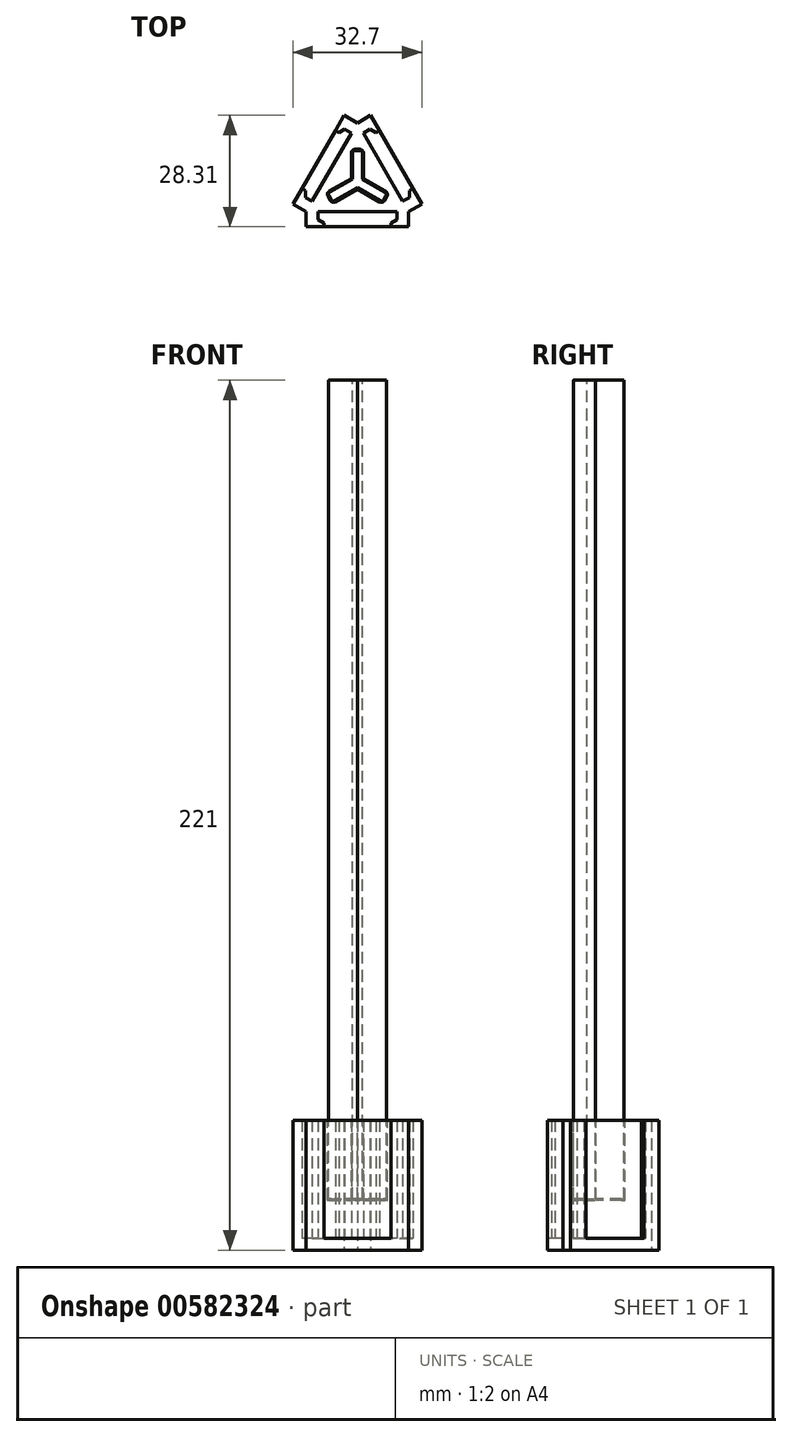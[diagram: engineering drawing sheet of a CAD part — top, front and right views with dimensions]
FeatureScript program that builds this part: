
annotation { "Feature Type Name" : "Feature", "Feature Type Description" : "" }
export const myFeature = defineFeature(function(context is Context, id is Id, definition is map)
    precondition{}
    {
        {
            var Q0;
            Q0=qCreatedBy(makeId("Top.planeOp"),FACE);
            var sketch = newSketch(context, id + "F0", { "sketchPlane" : qUnion([Q0])});
            skLineSegment(sketch, "E0", {"start": v(0, -7.5) * mm, "end": v(10, -7.5) * mm});
            skLineSegment(sketch, "E1", {"start": v(10, -7.5) * mm, "end": v(10, -9.5) * mm});
            skLineSegment(sketch, "E2", {"start": v(10, -9.5) * mm, "end": v(8.5, -10.37) * mm});
            skLineSegment(sketch, "E3", {"start": v(8.5, -10.37) * mm, "end": v(8.5, -11.37) * mm});
            skLineSegment(sketch, "E4", {"start": v(8.5, -11.37) * mm, "end": v(13, -11.37) * mm});
            skLineSegment(sketch, "E5", {"start": v(13, -11.37) * mm, "end": v(13, -7.5) * mm});
            skLineSegment(sketch, "E6.MirrorCS", {"start": v(-13, -11.37) * mm, "end": v(-13, -7.5) * mm});
            skLineSegment(sketch, "E7.MirrorCS", {"start": v(-10, -7.5) * mm, "end": v(-10, -9.5) * mm});
            skLineSegment(sketch, "E8.MirrorCS", {"start": v(0, -7.5) * mm, "end": v(-10, -7.5) * mm});
            skLineSegment(sketch, "E9.MirrorCS", {"start": v(-8.5, -10.37) * mm, "end": v(-8.5, -11.37) * mm});
            skLineSegment(sketch, "E10.MirrorCS", {"start": v(-10, -9.5) * mm, "end": v(-8.5, -10.37) * mm});
            skLineSegment(sketch, "E11.MirrorCS", {"start": v(-8.5, -11.37) * mm, "end": v(-13, -11.37) * mm});
            skLineSegment(sketch, "E12.1.0", {"start": v(6.5, 3.75) * mm, "end": v(11.5, -4.9) * mm});
            skLineSegment(sketch, "E12.1.1", {"start": v(1.5, 12.41) * mm, "end": v(3.23, 13.41) * mm});
            skLineSegment(sketch, "E12.1.2", {"start": v(11.5, -4.9) * mm, "end": v(13.23, -3.9) * mm});
            skLineSegment(sketch, "E12.1.3", {"start": v(14.1, -1.68) * mm, "end": v(16.35, -5.57) * mm});
            skLineSegment(sketch, "E12.1.4", {"start": v(16.35, -5.57) * mm, "end": v(13, -7.5) * mm});
            skLineSegment(sketch, "E12.1.5", {"start": v(5.6, 13.05) * mm, "end": v(3.35, 16.94) * mm});
            skLineSegment(sketch, "E12.1.6", {"start": v(6.5, 3.75) * mm, "end": v(1.5, 12.41) * mm});
            skLineSegment(sketch, "E12.1.7", {"start": v(3.35, 16.94) * mm, "end": v(0, 15.01) * mm});
            skLineSegment(sketch, "E12.1.8", {"start": v(13.23, -2.18) * mm, "end": v(14.1, -1.68) * mm});
            skLineSegment(sketch, "E12.1.9", {"start": v(3.23, 13.41) * mm, "end": v(4.73, 12.55) * mm});
            skLineSegment(sketch, "E12.1.10", {"start": v(13.23, -3.9) * mm, "end": v(13.23, -2.18) * mm});
            skLineSegment(sketch, "E12.1.11", {"start": v(4.73, 12.55) * mm, "end": v(5.6, 13.05) * mm});
            skLineSegment(sketch, "E12.2.0", {"start": v(-6.5, 3.75) * mm, "end": v(-1.5, 12.41) * mm});
            skLineSegment(sketch, "E12.2.1", {"start": v(-11.5, -4.9) * mm, "end": v(-13.23, -3.9) * mm});
            skLineSegment(sketch, "E12.2.2", {"start": v(-1.5, 12.41) * mm, "end": v(-3.23, 13.41) * mm});
            skLineSegment(sketch, "E12.2.3", {"start": v(-5.6, 13.05) * mm, "end": v(-3.35, 16.94) * mm});
            skLineSegment(sketch, "E12.2.4", {"start": v(-3.35, 16.94) * mm, "end": v(0, 15.01) * mm});
            skLineSegment(sketch, "E12.2.5", {"start": v(-14.1, -1.68) * mm, "end": v(-16.35, -5.57) * mm});
            skLineSegment(sketch, "E12.2.6", {"start": v(-6.5, 3.75) * mm, "end": v(-11.5, -4.9) * mm});
            skLineSegment(sketch, "E12.2.7", {"start": v(-16.35, -5.57) * mm, "end": v(-13, -7.5) * mm});
            skLineSegment(sketch, "E12.2.8", {"start": v(-4.73, 12.55) * mm, "end": v(-5.6, 13.05) * mm});
            skLineSegment(sketch, "E12.2.9", {"start": v(-13.23, -3.9) * mm, "end": v(-13.23, -2.18) * mm});
            skLineSegment(sketch, "E12.2.10", {"start": v(-3.23, 13.41) * mm, "end": v(-4.73, 12.55) * mm});
            skLineSegment(sketch, "E12.2.11", {"start": v(-13.23, -2.18) * mm, "end": v(-14.1, -1.68) * mm});
            skPoint(sketch, "E12.center", {"position": v(0, 0) * mm});
            skSolve(sketch);
        }
        {
            var Q0;
            Q0=makeQuery(id+"F0.imprint","IMPRINT",FACE,{"disambiguationData":[TD([[makeQuery(id+"F0.imprint","IMPRINT",EDGE,{"derivedFrom":sQuery(id+"F0.wireOp",EDGE,"E0")}),1.0]])]});
            extrude(context, id + "F1", {"entities" : qUnion([Q0]), "depth" : 30 * mm, "offsetDistance" : 25 * mm});
        }
        {
            var Q0;
            Q0=makeQuery(id+"F1.opExtrude","CAP_FACE",FACE,{"disambiguationData":[OSD([sQuery(id+"F0.wireOp",EDGE,"E0"),sQuery(id+"F0.wireOp",EDGE,"E1"),sQuery(id+"F0.wireOp",EDGE,"E2"),sQuery(id+"F0.wireOp",EDGE,"E3"),sQuery(id+"F0.wireOp",EDGE,"E4"),sQuery(id+"F0.wireOp",EDGE,"E5"),sQuery(id+"F0.wireOp",EDGE,"E6.MirrorCS"),sQuery(id+"F0.wireOp",EDGE,"E7.MirrorCS"),sQuery(id+"F0.wireOp",EDGE,"E8.MirrorCS"),sQuery(id+"F0.wireOp",EDGE,"E9.MirrorCS"),sQuery(id+"F0.wireOp",EDGE,"E10.MirrorCS"),sQuery(id+"F0.wireOp",EDGE,"E11.MirrorCS"),sQuery(id+"F0.wireOp",EDGE,"E12.1.0"),sQuery(id+"F0.wireOp",EDGE,"E12.1.1"),sQuery(id+"F0.wireOp",EDGE,"E12.1.2"),sQuery(id+"F0.wireOp",EDGE,"E12.1.3"),sQuery(id+"F0.wireOp",EDGE,"E12.1.4"),sQuery(id+"F0.wireOp",EDGE,"E12.1.5"),sQuery(id+"F0.wireOp",EDGE,"E12.1.6"),sQuery(id+"F0.wireOp",EDGE,"E12.1.7"),sQuery(id+"F0.wireOp",EDGE,"E12.1.8"),sQuery(id+"F0.wireOp",EDGE,"E12.1.9"),sQuery(id+"F0.wireOp",EDGE,"E12.1.10"),sQuery(id+"F0.wireOp",EDGE,"E12.1.11"),sQuery(id+"F0.wireOp",EDGE,"E12.2.0"),sQuery(id+"F0.wireOp",EDGE,"E12.2.1"),sQuery(id+"F0.wireOp",EDGE,"E12.2.2"),sQuery(id+"F0.wireOp",EDGE,"E12.2.3"),sQuery(id+"F0.wireOp",EDGE,"E12.2.4"),sQuery(id+"F0.wireOp",EDGE,"E12.2.5"),sQuery(id+"F0.wireOp",EDGE,"E12.2.6"),sQuery(id+"F0.wireOp",EDGE,"E12.2.7"),sQuery(id+"F0.wireOp",EDGE,"E12.2.8"),sQuery(id+"F0.wireOp",EDGE,"E12.2.9"),sQuery(id+"F0.wireOp",EDGE,"E12.2.10"),sQuery(id+"F0.wireOp",EDGE,"E12.2.11")])],"isStart":true});
            var sketch = newSketch(context, id + "F2", { "sketchPlane" : qUnion([Q0])});
            skLineSegment(sketch, "E13", {"start": v(-13, 11.37) * mm, "end": v(13, 11.37) * mm});
            skLineSegment(sketch, "E14", {"start": v(13, 11.37) * mm, "end": v(13, 7.5) * mm});
            skLineSegment(sketch, "E15", {"start": v(13, 7.5) * mm, "end": v(16.35, 5.57) * mm});
            skLineSegment(sketch, "E16", {"start": v(16.35, 5.57) * mm, "end": v(3.35, -16.94) * mm});
            skLineSegment(sketch, "E17", {"start": v(3.35, -16.94) * mm, "end": v(0, -15.01) * mm});
            skLineSegment(sketch, "E18", {"start": v(0, -15.01) * mm, "end": v(-3.35, -16.94) * mm});
            skLineSegment(sketch, "E19", {"start": v(-3.35, -16.94) * mm, "end": v(-16.35, 5.57) * mm});
            skLineSegment(sketch, "E20", {"start": v(-16.35, 5.57) * mm, "end": v(-13, 7.5) * mm});
            skLineSegment(sketch, "E21", {"start": v(-13, 7.5) * mm, "end": v(-13, 11.37) * mm});
            skSolve(sketch);
        }
        {
            var Q0;
            Q0 = qSketchRegion(id + "F2", true);
            extrude(context, id + "F3", {"entities" : qUnion([Q0]), "operationType" : NewBodyOperationType.ADD, "depth" : 3 * mm, "offsetDistance" : 25 * mm});
        }
        {
            var Q0;
            Q0=makeQuery(id+"F1.opExtrude","CAP_FACE",FACE,{"disambiguationData":[OSD([sQuery(id+"F0.wireOp",EDGE,"E0"),sQuery(id+"F0.wireOp",EDGE,"E1"),sQuery(id+"F0.wireOp",EDGE,"E2"),sQuery(id+"F0.wireOp",EDGE,"E3"),sQuery(id+"F0.wireOp",EDGE,"E4"),sQuery(id+"F0.wireOp",EDGE,"E5"),sQuery(id+"F0.wireOp",EDGE,"E6.MirrorCS"),sQuery(id+"F0.wireOp",EDGE,"E7.MirrorCS"),sQuery(id+"F0.wireOp",EDGE,"E8.MirrorCS"),sQuery(id+"F0.wireOp",EDGE,"E9.MirrorCS"),sQuery(id+"F0.wireOp",EDGE,"E10.MirrorCS"),sQuery(id+"F0.wireOp",EDGE,"E11.MirrorCS"),sQuery(id+"F0.wireOp",EDGE,"E12.1.0"),sQuery(id+"F0.wireOp",EDGE,"E12.1.1"),sQuery(id+"F0.wireOp",EDGE,"E12.1.2"),sQuery(id+"F0.wireOp",EDGE,"E12.1.3"),sQuery(id+"F0.wireOp",EDGE,"E12.1.4"),sQuery(id+"F0.wireOp",EDGE,"E12.1.5"),sQuery(id+"F0.wireOp",EDGE,"E12.1.6"),sQuery(id+"F0.wireOp",EDGE,"E12.1.7"),sQuery(id+"F0.wireOp",EDGE,"E12.1.8"),sQuery(id+"F0.wireOp",EDGE,"E12.1.9"),sQuery(id+"F0.wireOp",EDGE,"E12.1.10"),sQuery(id+"F0.wireOp",EDGE,"E12.1.11"),sQuery(id+"F0.wireOp",EDGE,"E12.2.0"),sQuery(id+"F0.wireOp",EDGE,"E12.2.1"),sQuery(id+"F0.wireOp",EDGE,"E12.2.2"),sQuery(id+"F0.wireOp",EDGE,"E12.2.3"),sQuery(id+"F0.wireOp",EDGE,"E12.2.4"),sQuery(id+"F0.wireOp",EDGE,"E12.2.5"),sQuery(id+"F0.wireOp",EDGE,"E12.2.6"),sQuery(id+"F0.wireOp",EDGE,"E12.2.7"),sQuery(id+"F0.wireOp",EDGE,"E12.2.8"),sQuery(id+"F0.wireOp",EDGE,"E12.2.9"),sQuery(id+"F0.wireOp",EDGE,"E12.2.10"),sQuery(id+"F0.wireOp",EDGE,"E12.2.11")])],"isStart":false});
            var sketch = newSketch(context, id + "F4", { "sketchPlane" : qUnion([Q0])});
            skLineSegment(sketch, "E22", {"start": v(-1.25, 0.72) * mm, "end": v(-1.25, 7.4) * mm});
            skLineSegment(sketch, "E23", {"start": v(-0.65, 8) * mm, "end": v(0.65, 8) * mm});
            skLineSegment(sketch, "E24", {"start": v(1.25, 7.4) * mm, "end": v(1.25, 0.72) * mm});
            skLineSegment(sketch, "E25.1.0", {"start": v(-6.6, -4.56) * mm, "end": v(-7.25, -3.44) * mm});
            skLineSegment(sketch, "E25.1.1", {"start": v(0, -1.44) * mm, "end": v(-5.78, -4.78) * mm});
            skLineSegment(sketch, "E25.1.2", {"start": v(-7.03, -2.62) * mm, "end": v(-1.25, 0.72) * mm});
            skLineSegment(sketch, "E25.2.0", {"start": v(7.25, -3.44) * mm, "end": v(6.6, -4.56) * mm});
            skLineSegment(sketch, "E25.2.1", {"start": v(1.25, 0.72) * mm, "end": v(7.03, -2.62) * mm});
            skLineSegment(sketch, "E25.2.2", {"start": v(5.78, -4.78) * mm, "end": v(0, -1.44) * mm});
            skPoint(sketch, "E25.center", {"position": v(0, 0) * mm});
            skPoint(sketch, "E26.visualSharp", {"position": v(1.25, 8) * mm});
            skArc(sketch, "E26.filletArc", {"start": v(1.25, 7.4) * mm, "mid": v(1.07, 7.82) * mm, "end": v(0.65, 8) * mm});
            skPoint(sketch, "E27.visualSharp", {"position": v(-1.25, 8) * mm});
            skArc(sketch, "E27.filletArc", {"start": v(-0.65, 8) * mm, "mid": v(-1.07, 7.82) * mm, "end": v(-1.25, 7.4) * mm});
            skPoint(sketch, "E28.visualSharp", {"position": v(-7.55, -2.92) * mm});
            skArc(sketch, "E28.filletArc", {"start": v(-7.03, -2.62) * mm, "mid": v(-7.31, -2.98) * mm, "end": v(-7.25, -3.44) * mm});
            skPoint(sketch, "E29.visualSharp", {"position": v(-6.3, -5.08) * mm});
            skArc(sketch, "E29.filletArc", {"start": v(-6.6, -4.56) * mm, "mid": v(-6.24, -4.84) * mm, "end": v(-5.78, -4.78) * mm});
            skPoint(sketch, "E30.visualSharp", {"position": v(6.3, -5.08) * mm});
            skArc(sketch, "E30.filletArc", {"start": v(5.78, -4.78) * mm, "mid": v(6.24, -4.84) * mm, "end": v(6.6, -4.56) * mm});
            skPoint(sketch, "E31.visualSharp", {"position": v(7.55, -2.92) * mm});
            skArc(sketch, "E31.filletArc", {"start": v(7.25, -3.44) * mm, "mid": v(7.31, -2.98) * mm, "end": v(7.03, -2.62) * mm});
            skSolve(sketch);
        }
        {
            var Q0;
            Q0 = qSketchRegion(id + "F4", true);
            var Q1;
            {var subQ0=sQuery(id+"F2.wireOp",EDGE,"E13");Q1=makeQuery(id+"F3.boolean.opBoolean","SPLIT",FACE,{"disambiguationData":[TD([makeQuery(id+"F1.opExtrude","SWEPT_FACE",FACE,{"disambiguationData":[OSD([sQuery(id+"F0.wireOp",EDGE,"E1")])]})])],"derivedFrom":makeQuery(id+"F3.opExtrude","CAP_FACE",FACE,{"disambiguationData":[OSD([subQ0,sQuery(id+"F2.wireOp",EDGE,"E14"),sQuery(id+"F2.wireOp",EDGE,"E15"),sQuery(id+"F2.wireOp",EDGE,"E16"),sQuery(id+"F2.wireOp",EDGE,"E17"),sQuery(id+"F2.wireOp",EDGE,"E18"),sQuery(id+"F2.wireOp",EDGE,"E19"),sQuery(id+"F2.wireOp",EDGE,"E20"),sQuery(id+"F2.wireOp",EDGE,"E21")])],"isStart":true})});}
            extrude(context, id + "F5", {"entities" : qUnion([Q0]), "oppositeDirection" : true, "depth" : 20 * mm, "offsetDistance" : 25 * mm, "hasSecondDirection" : true, "secondDirectionOppositeDirection" : false, "secondDirectionDepth" : (206 + 17 - 20 - 13 - 2) * mm, "secondDirectionBoundEntityFace" : qUnion([Q1]), "hasSecondDirectionOffset" : true, "secondDirectionOffsetDistance" : 100 * mm, "secondDirectionOffsetOppositeDirection" : true});
        }
        {
            var Q0;
            Q0=makeQuery(id+"F5.opExtrude","SWEPT_BODY",BODY,{"disambiguationData":[OSD([sQuery(id+"F4.wireOp",EDGE,"E22"),sQuery(id+"F4.wireOp",EDGE,"E23"),sQuery(id+"F4.wireOp",EDGE,"E24"),sQuery(id+"F4.wireOp",EDGE,"E25.1.0"),sQuery(id+"F4.wireOp",EDGE,"E25.1.1"),sQuery(id+"F4.wireOp",EDGE,"E25.1.2"),sQuery(id+"F4.wireOp",EDGE,"E25.2.0"),sQuery(id+"F4.wireOp",EDGE,"E25.2.1"),sQuery(id+"F4.wireOp",EDGE,"E25.2.2")])]});
            var Q1;
            Q1=makeQuery(id+"F1.opExtrude","SWEPT_BODY",BODY,{"disambiguationData":[OSD([sQuery(id+"F0.wireOp",EDGE,"E0"),sQuery(id+"F0.wireOp",EDGE,"E1"),sQuery(id+"F0.wireOp",EDGE,"E2"),sQuery(id+"F0.wireOp",EDGE,"E3"),sQuery(id+"F0.wireOp",EDGE,"E4"),sQuery(id+"F0.wireOp",EDGE,"E5"),sQuery(id+"F0.wireOp",EDGE,"E6.MirrorCS"),sQuery(id+"F0.wireOp",EDGE,"E7.MirrorCS"),sQuery(id+"F0.wireOp",EDGE,"E8.MirrorCS"),sQuery(id+"F0.wireOp",EDGE,"E9.MirrorCS"),sQuery(id+"F0.wireOp",EDGE,"E10.MirrorCS"),sQuery(id+"F0.wireOp",EDGE,"E11.MirrorCS"),sQuery(id+"F0.wireOp",EDGE,"E12.1.0"),sQuery(id+"F0.wireOp",EDGE,"E12.1.1"),sQuery(id+"F0.wireOp",EDGE,"E12.1.2"),sQuery(id+"F0.wireOp",EDGE,"E12.1.3"),sQuery(id+"F0.wireOp",EDGE,"E12.1.4"),sQuery(id+"F0.wireOp",EDGE,"E12.1.5"),sQuery(id+"F0.wireOp",EDGE,"E12.1.6"),sQuery(id+"F0.wireOp",EDGE,"E12.1.7"),sQuery(id+"F0.wireOp",EDGE,"E12.1.8"),sQuery(id+"F0.wireOp",EDGE,"E12.1.9"),sQuery(id+"F0.wireOp",EDGE,"E12.1.10"),sQuery(id+"F0.wireOp",EDGE,"E12.1.11"),sQuery(id+"F0.wireOp",EDGE,"E12.2.0"),sQuery(id+"F0.wireOp",EDGE,"E12.2.1"),sQuery(id+"F0.wireOp",EDGE,"E12.2.2"),sQuery(id+"F0.wireOp",EDGE,"E12.2.3"),sQuery(id+"F0.wireOp",EDGE,"E12.2.4"),sQuery(id+"F0.wireOp",EDGE,"E12.2.5"),sQuery(id+"F0.wireOp",EDGE,"E12.2.6"),sQuery(id+"F0.wireOp",EDGE,"E12.2.7"),sQuery(id+"F0.wireOp",EDGE,"E12.2.8"),sQuery(id+"F0.wireOp",EDGE,"E12.2.9"),sQuery(id+"F0.wireOp",EDGE,"E12.2.10"),sQuery(id+"F0.wireOp",EDGE,"E12.2.11")])]});
            booleanBodies(context, id + "F6", {"operationType" : BooleanOperationType.SUBTRACTION, "tools" : qUnion([Q0]), "targets" : qUnion([Q1]), "offset" : true, "offsetAll" : true, "offsetDistance" : 0.3 * mm, "keepTools" : true});
        }
    });
